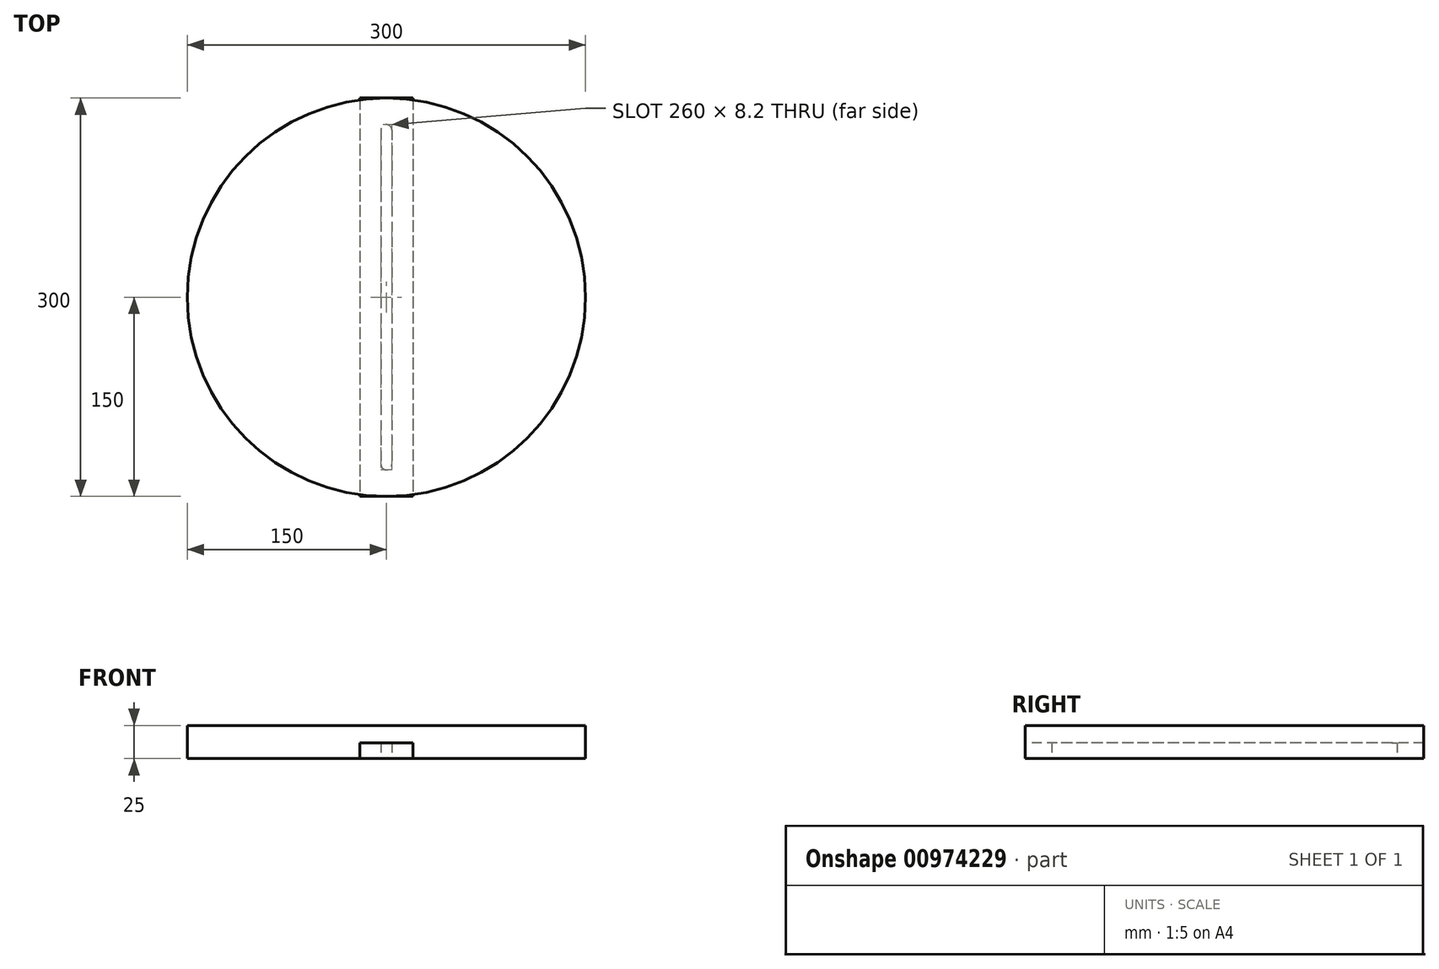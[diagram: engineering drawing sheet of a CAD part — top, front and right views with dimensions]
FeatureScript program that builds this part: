
annotation { "Feature Type Name" : "Feature", "Feature Type Description" : "" }
export const myFeature = defineFeature(function(context is Context, id is Id, definition is map)
    precondition{}
    {
        {
            var Q0;
            Q0=qCreatedBy(makeId("Top.planeOp"),FACE);
            var sketch = newSketch(context, id + "F0", { "sketchPlane" : qUnion([Q0])});
            skLineSegment(sketch, "E0.bottom", {"start": v(-20, 150) * mm, "end": v(20, 150) * mm});
            skLineSegment(sketch, "E0.top", {"start": v(-20, -150) * mm, "end": v(20, -150) * mm});
            skLineSegment(sketch, "E0.left", {"start": v(-20, 150) * mm, "end": v(-20, -150) * mm});
            skLineSegment(sketch, "E0.right", {"start": v(20, 150) * mm, "end": v(20, -150) * mm});
            skLineSegment(sketch, "E1.bottom", {"start": v(0, 130) * mm, "end": v(0, 130) * mm});
            skLineSegment(sketch, "E1.top", {"start": v(0, -130) * mm, "end": v(0, -130) * mm});
            skLineSegment(sketch, "E1.left", {"start": v(-4.1, 125.9) * mm, "end": v(-4.1, -125.9) * mm});
            skLineSegment(sketch, "E1.right", {"start": v(4.1, 125.9) * mm, "end": v(4.1, -125.9) * mm});
            skLineSegment(sketch, "E2", {"start": v(0, 150) * mm, "end": v(0, -150) * mm, "construction": true});
            skLineSegment(sketch, "E3", {"start": v(-20, 0) * mm, "end": v(20, 0) * mm, "construction": true});
            skPoint(sketch, "E4.visualSharp", {"position": v(-4.1, 130) * mm});
            skArc(sketch, "E4.filletArc", {"start": v(0, 130) * mm, "mid": v(-2.9, 128.8) * mm, "end": v(-4.1, 125.9) * mm});
            skPoint(sketch, "E5.visualSharp", {"position": v(4.1, 130) * mm});
            skArc(sketch, "E5.filletArc", {"start": v(4.1, 125.9) * mm, "mid": v(2.9, 128.8) * mm, "end": v(0, 130) * mm});
            skPoint(sketch, "E6.visualSharp", {"position": v(4.1, -130) * mm});
            skArc(sketch, "E6.filletArc", {"start": v(0, -130) * mm, "mid": v(2.9, -128.8) * mm, "end": v(4.1, -125.9) * mm});
            skPoint(sketch, "E7.visualSharp", {"position": v(-4.1, -130) * mm});
            skArc(sketch, "E7.filletArc", {"start": v(-4.1, -125.9) * mm, "mid": v(-2.9, -128.8) * mm, "end": v(0, -130) * mm});
            skSolve(sketch);
        }
        {
            var Q0;
            Q0 = qSketchRegion(id + "F0", true);
            extrude(context, id + "F1", {"entities" : qUnion([Q0]), "depth" : 12 * mm, "offsetDistance" : 25 * mm});
        }
        {
            var Q0;
            Q0=qCreatedBy(makeId("Top.planeOp"),FACE);
            var sketch = newSketch(context, id + "F2", { "sketchPlane" : qUnion([Q0])});
            skCircle(sketch, "E8", {"center": v(0, 0) * mm, "radius": 150 * mm});
            skSolve(sketch);
        }
        {
            var Q0;
            Q0 = qSketchRegion(id + "F2", true);
            extrude(context, id + "F3", {"entities" : qUnion([Q0]), "depth" : 25 * mm, "offsetDistance" : 25 * mm});
        }
    });
